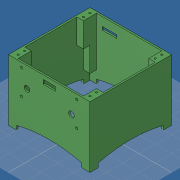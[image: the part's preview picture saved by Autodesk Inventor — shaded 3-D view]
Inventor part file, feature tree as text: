
AUTODESK INVENTOR PART (.ipt)
format: ipt  version: 2019 (Build 230136000, 136)  size: 233,472 bytes
history: native  units: mm
features: extrude x8, sketch x6, projected_geometry x2, hole x1
ambient origin geometry x8: Origin, YZ Plane, XZ Plane, XY Plane, X Axis, Y Axis, Z Axis, Center Point
bodies: Volumenkörper1 (feature_tree)
feature tree (17):
  extrude  "Extrusion1"  Depth=100.0mm
  extrude  "Extrusion2"  Depth=5.0mm
  extrude  "Extrusion3"  Depth=50.0mm TaperAngle=0.0deg
  sketch  "Skizze9"  dims[d29=10.0mm d30=10.0mm]
  extrude  "Extrusion9"  Depth=50.0mm TaperAngle=0.0deg
  extrude  "Extrusion10"  Depth=10.0mm
  extrude  "Extrusion11"  Depth=5.0mm
  hole  "Bohrung3"  [1 undecoded]
  extrude  "Extrusion12"  Depth=7.0mm
  extrude  "Extrusion8"  Depth=7.0mm
  sketch  "Skizze1"  dims[d0=100.0mm d1=100.0mm]
  sketch  "Skizze2"  dims[d2=75.0mm d3=0.0mm d4=5.0mm]
  sketch  "Skizze3"  dims[d6=80.0mm d7=50.0mm d8=0.0mm]
  sketch  "Skizze8"  dims[d9=5.0mm d11=80.0mm d12=50.0mm d13=0.0mm]
  sketch  "Skizze10"  dims[d57=15.0mm d58=5.0mm d59=5.0mm d60=7.0mm d61=7.0mm d62=35.0mm d63=0.0mm d64=3.0mm d65=2.0mm d67=10.0mm d68=0.0mm d69=60.0mm d70=0.0mm d71=30.0mm d72=0.0mm d73=2.2mm d74=6.0mm d75=4.0mm d76=2.0mm d77=90.0deg d78=6.0mm d79=0.0mm d81=8.0mm d82=8.0mm d83=6.5mm d84=15.5mm d85=18.0mm d86=5.5mm d87=2.5mm d89=15.0mm d90=18.0mm d91=4.0mm d92=15.5mm d93=40.0mm d94=0.0mm]
  projected_geometry  "Projizierte Kontur4"
  projected_geometry  "Projizierte Kontur5"
note: 1 required parameter value undecoded (feature->parameter linkage not recoverable at this tier; creation-order binding heuristic only, values carry confidence <= 0.55)
